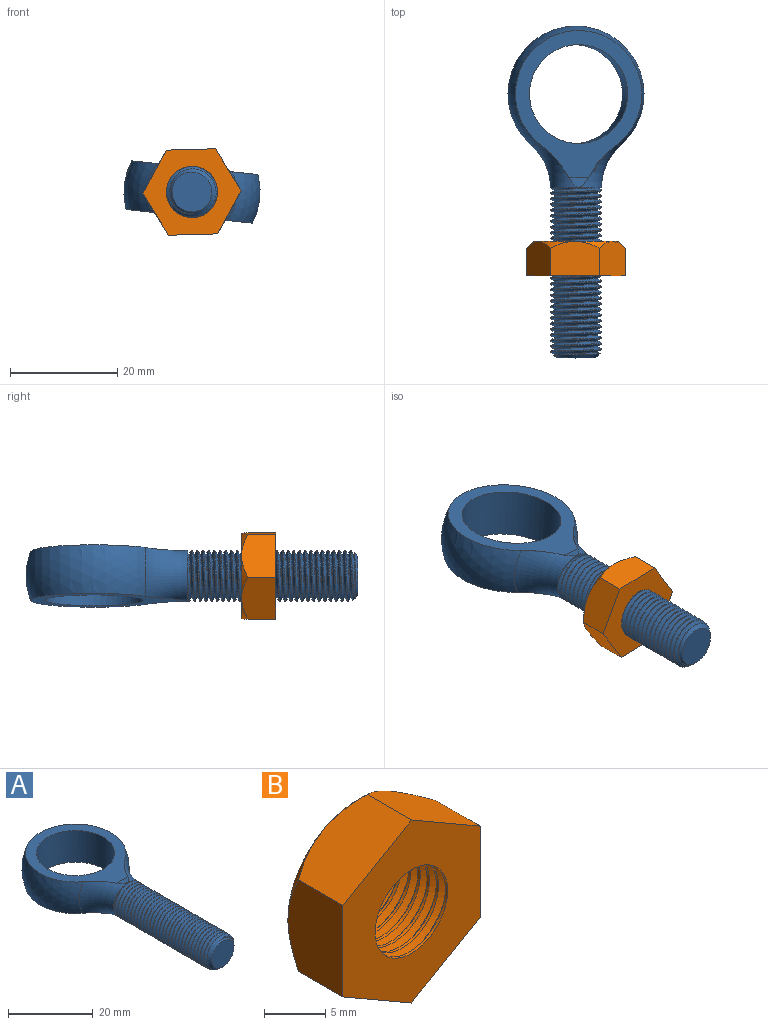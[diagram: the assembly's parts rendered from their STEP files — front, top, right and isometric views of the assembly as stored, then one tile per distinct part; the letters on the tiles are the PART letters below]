
ASSEMBLY  parts=2 mates=1
PART A: 15 faces, bbox 33.5x62.6x33.5 mm
  f0: torus R=15.24mm, axis (0,-1,0), area 100.6mm2, adj f8,f9,f10,f11,f12,f13
  f1: cylinder r=4.76mm len=30.69mm, axis (0,1,0), area 115mm2, adj f2,f4,f6,f7
  f2: cone r=4.76mm half-angle=45deg, axis (0,1,0), area 26mm2, adj f1,f3,f4,f5,f6
  f3: plane 7.41x7.41mm, normal (0,-1,0), area 43.1mm2, adj f2
  f4: bspline ~32.28x9.53mm, area 648.2mm2, adj f1,f2,f5,f9
  f5: bspline ~31.75x8.15mm, area 100.8mm2, adj f2,f4,f6,f9
  f6: bspline ~31.88x9.53mm, area 648.5mm2, adj f1,f2,f5,f9
  f7: torus R=15.24mm, axis (0,-1,0), area 100.6mm2, adj f1,f8,f9,f10,f11,f12,f13
  f8: sphere r=12.7mm, area 567.7mm2, adj f0,f7,f10,f12
  f9: plane 9.95x9.95mm, normal (0,-1,0), area 9.7mm2, adj f0,f4,f5,f6,f7
  f10: plane 28.02x24.23mm, normal (0,0,1), area 201.2mm2, adj f0,f7,f8,f11,f14
  f11: plane 4.14x2.26mm, normal (0,0.11,0.99), area 4.1mm2, adj f0,f7,f10
  f12: plane 28.03x24.24mm, normal (0,0,-1), area 201.2mm2, adj f0,f7,f8,f13,f14
  f13: plane 4.14x2.26mm, normal (0,0.11,-0.99), area 4.1mm2, adj f0,f7,f12
  f14: cylinder r=9.22mm len=18.45mm, axis (0,0,1), area 528.4mm2, adj f10,f12
PART B: 39 faces, bbox 18.3x6.4x18.3 mm
  f0: plane 18.33x15.88mm, normal (0,-1,0), area 163.1mm2, adj f2,f3,f4,f5,f6,f7,f37
  f1: plane 15.88x15.88mm, normal (0,1,0), area 128mm2, adj f8,f9,f10,f11,f12,f13,f38
  f2: plane 7.94x6.36mm, normal (0.5,0,-0.87), area 54.3mm2, adj f0,f3,f7,f11,f12
  f3: plane 7.94x6.36mm, normal (-0.5,0,-0.87), area 54.3mm2, adj f0,f2,f4,f10,f11
  f4: plane 9.18x6.36mm, normal (-1,0,0), area 54.3mm2, adj f0,f3,f5,f9,f10
  f5: plane 7.94x6.36mm, normal (-0.5,0,0.87), area 54.3mm2, adj f0,f4,f6,f8,f9
  f6: plane 7.94x6.36mm, normal (0.5,0,0.87), area 54.3mm2, adj f0,f5,f7,f8,f13
  f7: plane 9.18x6.36mm, normal (1,0,0), area 54.3mm2, adj f0,f2,f6,f12,f13
  f8: cone r=7.94mm half-angle=45deg, axis (0,-1,0), area 4.8mm2, adj f1,f5,f6
  f9: cone r=7.94mm half-angle=45deg, axis (0,-1,0), area 4.8mm2, adj f1,f4,f5
  f10: cone r=7.94mm half-angle=45deg, axis (0,-1,0), area 4.8mm2, adj f1,f3,f4
  f11: cone r=7.94mm half-angle=45deg, axis (0,-1,0), area 4.8mm2, adj f1,f2,f3
  f12: cone r=7.94mm half-angle=45deg, axis (0,-1,0), area 4.8mm2, adj f1,f2,f7
  f13: cone r=7.94mm half-angle=45deg, axis (0,-1,0), area 4.8mm2, adj f1,f6,f7
  f14: cone r=4.76mm half-angle=60deg, axis (0,-1,0), area 8mm2, adj f15,f38
  f15: cylinder r=4.76mm len=9.53mm, axis (0,1,0), area 4mm2, adj f14,f16
  f16: cone r=4.19mm half-angle=60deg, axis (0,1,0), area 18.6mm2, adj f15,f17
  f17: cylinder r=4.19mm len=8.38mm, axis (0,1,0), area 7mm2, adj f16,f18
  f18: cone r=4.76mm half-angle=60deg, axis (0,-1,0), area 18.6mm2, adj f17,f19
  f19: cylinder r=4.76mm len=9.53mm, axis (0,1,0), area 4mm2, adj f18,f20
  f20: cone r=4.19mm half-angle=60deg, axis (0,1,0), area 18.6mm2, adj f19,f21
  f21: cylinder r=4.19mm len=8.38mm, axis (0,1,0), area 7mm2, adj f20,f22
  f22: cone r=4.76mm half-angle=60deg, axis (0,-1,0), area 18.6mm2, adj f21,f23
  f23: cylinder r=4.76mm len=9.53mm, axis (0,1,0), area 4mm2, adj f22,f24
  f24: cone r=4.19mm half-angle=60deg, axis (0,1,0), area 18.6mm2, adj f23,f25
  f25: cylinder r=4.19mm len=8.38mm, axis (0,1,0), area 7mm2, adj f24,f26
  f26: cone r=4.76mm half-angle=60deg, axis (0,-1,0), area 18.6mm2, adj f25,f27
  f27: cylinder r=4.76mm len=9.53mm, axis (0,1,0), area 4mm2, adj f26,f28
  f28: cone r=4.19mm half-angle=60deg, axis (0,1,0), area 18.6mm2, adj f27,f29
  f29: cylinder r=4.19mm len=8.38mm, axis (0,1,0), area 7mm2, adj f28,f30
  f30: cone r=4.76mm half-angle=60deg, axis (0,-1,0), area 18.6mm2, adj f29,f31
  f31: cylinder r=4.76mm len=9.53mm, axis (0,1,0), area 4mm2, adj f30,f32
  f32: cone r=4.19mm half-angle=60deg, axis (0,1,0), area 18.6mm2, adj f31,f33
  f33: cylinder r=4.19mm len=8.38mm, axis (0,1,0), area 7mm2, adj f32,f34
  f34: cone r=4.76mm half-angle=60deg, axis (0,-1,0), area 18.6mm2, adj f33,f35
  f35: cylinder r=4.76mm len=9.53mm, axis (0,1,0), area 4mm2, adj f34,f36
  f36: cone r=4.19mm half-angle=60deg, axis (0,1,0), area 18.6mm2, adj f35,f37
  f37: cylinder r=4.19mm len=8.38mm, axis (0,1,0), area 7mm2, adj f0,f36
  f38: cone r=4.53mm half-angle=45deg, axis (0,1,0), area 8mm2, adj f1,f14
PLACE A rot(axis=(0,-1,0),173.8deg) t=(15.7,-6.87,-31.16)mm
PLACE B rot(axis=(0,-1,0),31.6deg) t=(15.7,-23.25,-31.16)mm
MATE cylindrical B.f8 <-> A.f1  axis (0,-1,0) through (15.7,-23.25,-31.16)mm
